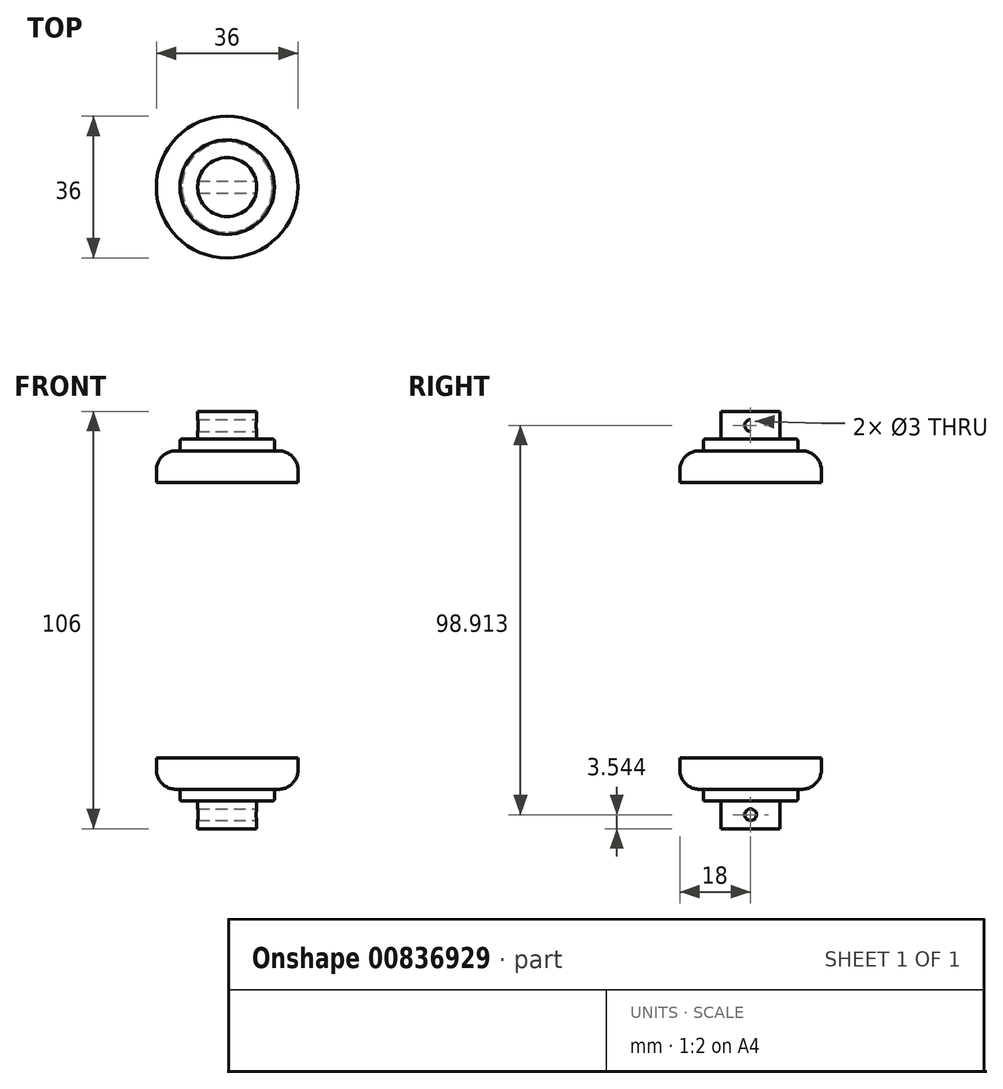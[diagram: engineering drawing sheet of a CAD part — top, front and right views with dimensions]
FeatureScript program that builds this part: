
annotation { "Feature Type Name" : "Feature", "Feature Type Description" : "" }
export const myFeature = defineFeature(function(context is Context, id is Id, definition is map)
    precondition{}
    {
        {
            var Q0;
            Q0=qCreatedBy(makeId("Front.planeOp"),FACE);
            var sketch = newSketch(context, id + "F0", { "sketchPlane" : qUnion([Q0])});
            skLineSegment(sketch, "E0", {"start": v(0, 0) * mm, "end": v(0, -87.28) * mm});
            skLineSegment(sketch, "E1.bottom", {"start": v(0, 0) * mm, "end": v(18, 0) * mm});
            skLineSegment(sketch, "E1.top", {"start": v(0, 8) * mm, "end": v(13, 8) * mm});
            skLineSegment(sketch, "E1.left", {"start": v(0, 0) * mm, "end": v(0, 8) * mm});
            skLineSegment(sketch, "E1.right", {"start": v(18, 0) * mm, "end": v(18, 3) * mm});
            skLineSegment(sketch, "E2.bottom", {"start": v(0, 0) * mm, "end": v(15, 0) * mm});
            skLineSegment(sketch, "E2.top", {"start": v(0, -70) * mm, "end": v(15, -70) * mm});
            skLineSegment(sketch, "E2.left", {"start": v(0, 0) * mm, "end": v(0, -70) * mm});
            skLineSegment(sketch, "E2.right", {"start": v(15, 0) * mm, "end": v(15, -70) * mm});
            skLineSegment(sketch, "E3.bottom", {"start": v(0, -70) * mm, "end": v(18, -70) * mm});
            skLineSegment(sketch, "E3.top", {"start": v(0, -78) * mm, "end": v(13, -78) * mm});
            skLineSegment(sketch, "E3.left", {"start": v(0, -70) * mm, "end": v(0, -78) * mm});
            skLineSegment(sketch, "E3.right", {"start": v(18, -70) * mm, "end": v(18, -73) * mm});
            skPoint(sketch, "E4.visualSharp", {"position": v(18, 8) * mm});
            skArc(sketch, "E4.filletArc", {"start": v(18, 3) * mm, "mid": v(16.54, 6.54) * mm, "end": v(13, 8) * mm});
            skPoint(sketch, "E5.visualSharp", {"position": v(18, -78) * mm});
            skArc(sketch, "E5.filletArc", {"start": v(13, -78) * mm, "mid": v(16.54, -76.54) * mm, "end": v(18, -73) * mm});
            skLineSegment(sketch, "E6", {"start": v(0, 8) * mm, "end": v(0, 48.38) * mm, "construction": true});
            skLineSegment(sketch, "E7", {"start": v(0, -78) * mm, "end": v(0, -100.45) * mm, "construction": true});
            skSolve(sketch);
        }
        {
            var Q0;
            Q0=makeQuery(id+"F0.imprint","IMPRINT",FACE,{"disambiguationData":[TD([[makeQuery(id+"F0.imprint","IMPRINT",EDGE,{"derivedFrom":sQuery(id+"F0.wireOp",EDGE,"E3.top")}),1.0]])]});
            var Q1;
            Q1=makeQuery(id+"F0.imprint","IMPRINT",FACE,{"disambiguationData":[TD([[makeQuery(id+"F0.imprint","IMPRINT",EDGE,{"derivedFrom":sQuery(id+"F0.wireOp",EDGE,"E2.bottom")}),-1.0]])]});
            var Q2;
            Q2=makeQuery(id+"F0.imprint","IMPRINT",FACE,{"disambiguationData":[TD([[makeQuery(id+"F0.imprint","IMPRINT",EDGE,{"derivedFrom":sQuery(id+"F0.wireOp",EDGE,"E1.bottom")}),1.0]])]});
            var Q3;
            Q3=sQuery(id+"F0.wireOp",EDGE,"E2.left");
            revolve(context, id + "F1", {"surfaceOperationType" : NewSurfaceOperationType.NEW, "entities" : qUnion([Q0, Q1, Q2]), "axis" : qUnion([Q3]), "revolveType" : RevolveType.FULL});
        }
        {
            var Q0;
            Q0=makeQuery(id+"F1.opRevolve","SWEPT_FACE",FACE,{"disambiguationData":[OSD([sQuery(id+"F0.wireOp",EDGE,"E1.top")])]});
            var sketch = newSketch(context, id + "F2", { "sketchPlane" : qUnion([Q0])});
            skCircle(sketch, "E8", {"center": v(0, 0) * mm, "radius": 12 * mm});
            skCircle(sketch, "E9", {"center": v(0, 0) * mm, "radius": 7.5 * mm});
            skSolve(sketch);
        }
        {
            var Q0;
            Q0=makeQuery(id+"F2.imprint","IMPRINT",FACE,{"disambiguationData":[TD([[makeQuery(id+"F2.imprint","IMPRINT",EDGE,{"derivedFrom":sQuery(id+"F2.wireOp",EDGE,"E8")}),1.0]])]});
            extrude(context, id + "F3", {"entities" : qUnion([Q0]), "depth" : 3 * mm, "offsetDistance" : 25 * mm});
        }
        {
            var Q0;
            Q0=makeQuery(id+"F3.opExtrude","CAP_EDGE",EDGE,{"disambiguationData":[OSD([sQuery(id+"F2.wireOp",EDGE,"E8")])],"isStart":false});
            fillet(context, id + "F4", {"entities" : qUnion([Q0]), "radius" : 0.5 * mm, "tangentPropagation" : true, "allowEdgeOverflow" : false});
        }
        {
            var Q0;
            Q0=makeQuery(id+"F3.opExtrude","CAP_EDGE",EDGE,{"disambiguationData":[OSD([sQuery(id+"F2.wireOp",EDGE,"E8")])],"isStart":true});
            fillet(context, id + "F5", {"entities" : qUnion([Q0]), "radius" : 0.5 * mm, "tangentPropagation" : true, "allowEdgeOverflow" : false});
        }
        {
            var Q0;
            Q0=makeQuery(id+"F2.imprint","IMPRINT",FACE,{"disambiguationData":[TD([[makeQuery(id+"F2.imprint","IMPRINT",EDGE,{"derivedFrom":sQuery(id+"F2.wireOp",EDGE,"E9")}),1.0]])]});
            extrude(context, id + "F6", {"entities" : qUnion([Q0]), "depth" : 10 * mm, "offsetDistance" : 25 * mm});
        }
        {
            var Q0;
            Q0=qCreatedBy(makeId("Right.planeOp"),FACE);
            cPlane(context, id + "F7", {"entities" : qUnion([Q0]), "cplaneType" : CPlaneType.OFFSET, "offset" : 40 * mm, "width" : 150 * mm, "height" : 150 * mm});
        }
        {
            var Q0;
            Q0=qCreatedBy(id+"F7.planeOp",FACE);
            var sketch = newSketch(context, id + "F8", { "sketchPlane" : qUnion([Q0])});
            skCircle(sketch, "E10", {"center": v(0, 14.46) * mm, "radius": 1.5 * mm});
            skSolve(sketch);
        }
        {
            var Q0;
            Q0=makeQuery(id+"F8.imprint","IMPRINT",FACE,{"disambiguationData":[TD([[makeQuery(id+"F8.imprint","IMPRINT",EDGE,{"derivedFrom":sQuery(id+"F8.wireOp",EDGE,"E10")}),1.0]])]});
            extrude(context, id + "F9", {"entities" : qUnion([Q0]), "operationType" : NewBodyOperationType.REMOVE, "endBound" : BoundingType.THROUGH_ALL, "oppositeDirection" : true, "depth" : 25 * mm, "offsetDistance" : 25 * mm});
        }
        {
            var Q0;
            Q0=qCreatedBy(makeId("Top.planeOp"),FACE);
            cPlane(context, id + "F10", {"entities" : qUnion([Q0]), "cplaneType" : CPlaneType.OFFSET, "offset" : 35 * mm, "oppositeDirection" : true, "width" : 150 * mm, "height" : 150 * mm});
        }
        {
            var Q0;
            Q0=makeQuery(id+"F3.opExtrude","SWEPT_BODY",BODY,{"disambiguationData":[OSD([sQuery(id+"F2.wireOp",EDGE,"E8"),sQuery(id+"F2.wireOp",EDGE,"E9")])]});
            var Q1;
            Q1=makeQuery(id+"F6.opExtrude","SWEPT_BODY",BODY,{"disambiguationData":[OSD([sQuery(id+"F2.wireOp",EDGE,"E9")])]});
            var Q2;
            Q2=qCreatedBy(id+"F10.planeOp",FACE);
            mirror(context, id + "F11", {"operationType" : NewBodyOperationType.ADD, "entities" : qUnion([Q0, Q1]), "mirrorPlane" : qUnion([Q2])});
        }
    });
